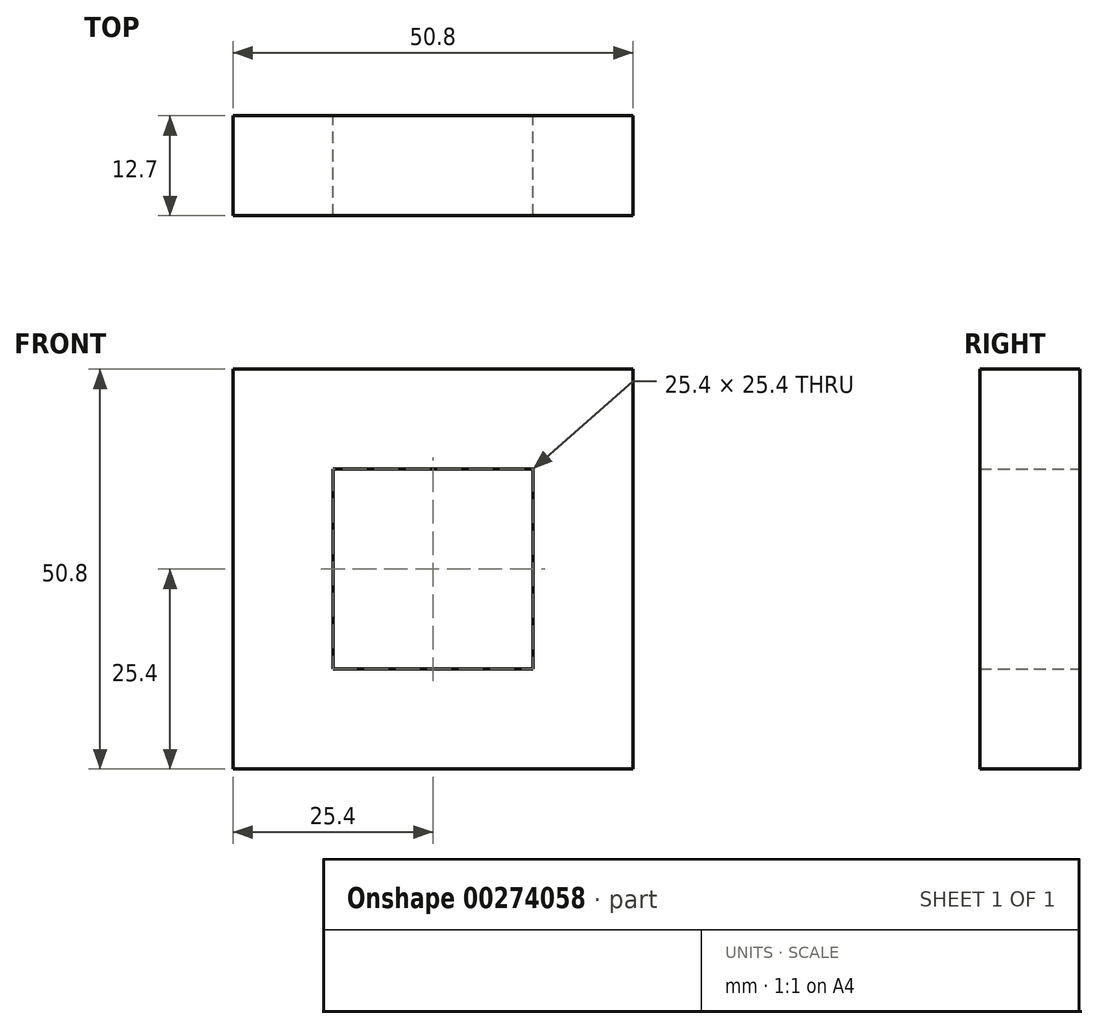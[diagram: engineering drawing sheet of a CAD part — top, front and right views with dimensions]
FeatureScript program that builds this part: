
annotation { "Feature Type Name" : "Feature", "Feature Type Description" : "" }
export const myFeature = defineFeature(function(context is Context, id is Id, definition is map)
    precondition{}
    {
        {
            var Q0;
            Q0=qCreatedBy(makeId("Front.planeOp"),FACE);
            var sketch = newSketch(context, id + "F0", { "sketchPlane" : qUnion([Q0])});
            skLineSegment(sketch, "E0.bottom", {"start": v(-25.4, 25.4) * mm, "end": v(25.4, 25.4) * mm});
            skLineSegment(sketch, "E0.top", {"start": v(-25.4, -25.4) * mm, "end": v(25.4, -25.4) * mm});
            skLineSegment(sketch, "E0.left", {"start": v(-25.4, 25.4) * mm, "end": v(-25.4, -25.4) * mm});
            skLineSegment(sketch, "E0.right", {"start": v(25.4, 25.4) * mm, "end": v(25.4, -25.4) * mm});
            skLineSegment(sketch, "E1.bottom", {"start": v(-12.7, 12.7) * mm, "end": v(12.7, 12.7) * mm});
            skLineSegment(sketch, "E1.top", {"start": v(-12.7, -12.7) * mm, "end": v(12.7, -12.7) * mm});
            skLineSegment(sketch, "E1.left", {"start": v(-12.7, 12.7) * mm, "end": v(-12.7, -12.7) * mm});
            skLineSegment(sketch, "E1.right", {"start": v(12.7, 12.7) * mm, "end": v(12.7, -12.7) * mm});
            skPoint(sketch, "E1.middle", {"position": v(0, 0) * mm});
            skSolve(sketch);
        }
        {
            var Q0;
            Q0=makeQuery(id+"F0.imprint","IMPRINT",FACE,{"disambiguationData":[TD([[makeQuery(id+"F0.imprint","IMPRINT",EDGE,{"derivedFrom":sQuery(id+"F0.wireOp",EDGE,"E0.bottom")}),-1.0]])]});
            var Q1;
            Q1=makeQuery(id+"F0.imprint","IMPRINT",FACE,{"disambiguationData":[TD([[makeQuery(id+"F0.imprint","IMPRINT",EDGE,{"derivedFrom":sQuery(id+"F0.wireOp",EDGE,"h7j9EmbP-waNi-Yu88-dRFL-SoBdgT9TmfJ6")}),1.0]])]});
            extrude(context, id + "F1", {"entities" : qUnion([Q0, Q1]), "depth" : 12.7 * mm});
        }
    });
